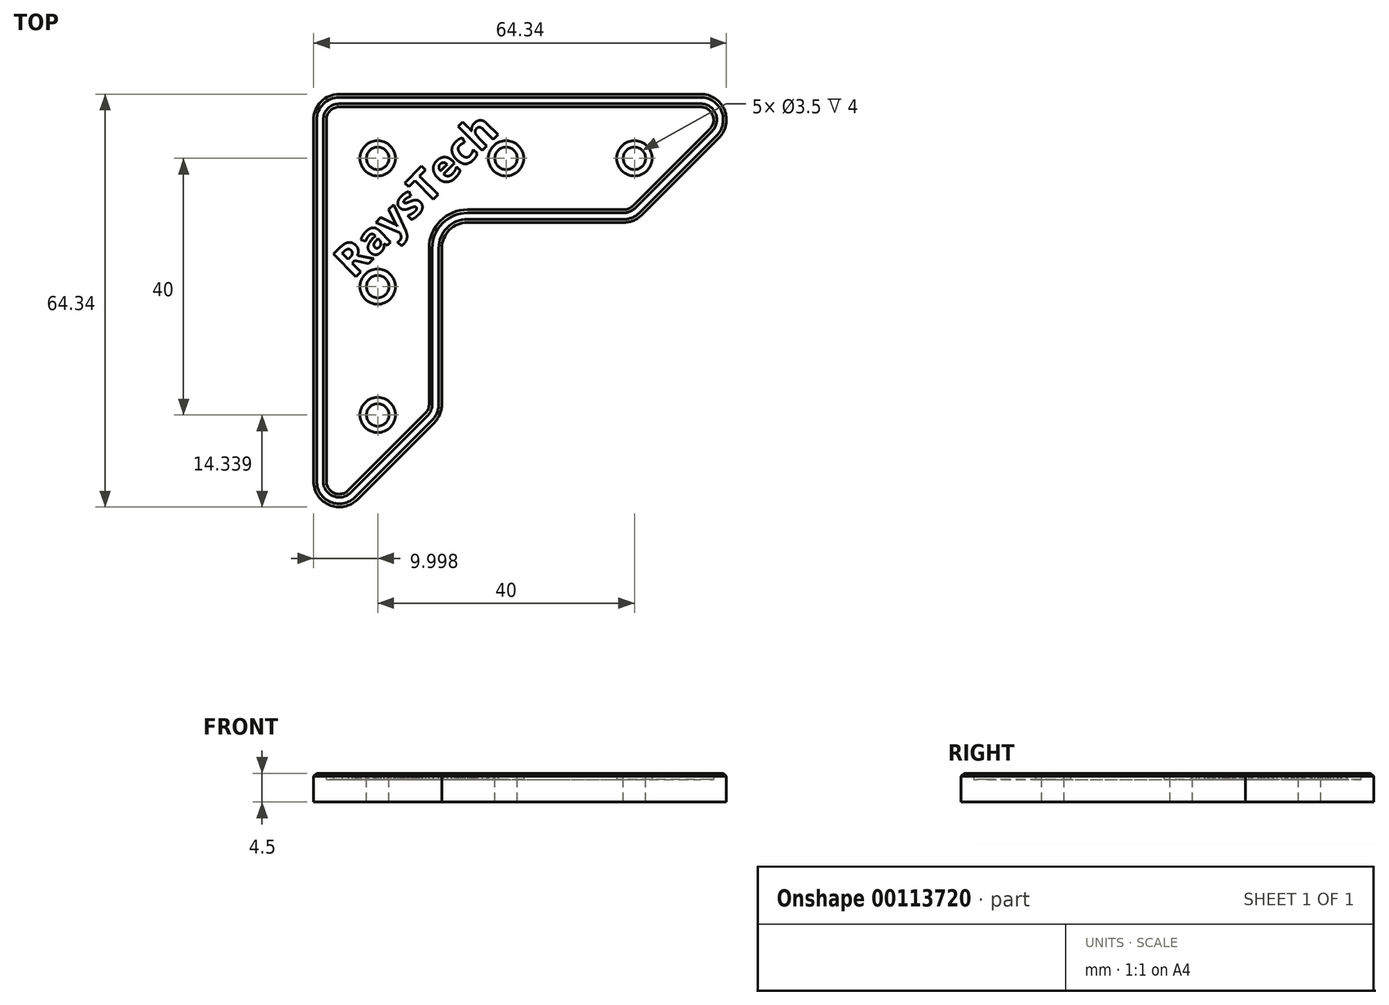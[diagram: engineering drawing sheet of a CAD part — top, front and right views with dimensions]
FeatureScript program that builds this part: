
annotation { "Feature Type Name" : "Feature", "Feature Type Description" : "" }
export const myFeature = defineFeature(function(context is Context, id is Id, definition is map)
    precondition{}
    {
        {
            var Q0;
            Q0=qCreatedBy(makeId("Top.planeOp"),FACE);
            var sketch = newSketch(context, id + "F0", { "sketchPlane" : qUnion([Q0])});
            skLineSegment(sketch, "E0", {"start": v(-45.73, 7.88) * mm, "end": v(24.27, 7.88) * mm});
            skLineSegment(sketch, "E1", {"start": v(24.27, 7.88) * mm, "end": v(4.27, -12.12) * mm});
            skLineSegment(sketch, "E2", {"start": v(-25.73, -42.12) * mm, "end": v(-45.73, -62.12) * mm});
            skLineSegment(sketch, "E3", {"start": v(-45.73, -62.12) * mm, "end": v(-45.73, 7.88) * mm});
            skLineSegment(sketch, "E4", {"start": v(-25.73, -42.12) * mm, "end": v(-25.73, -12.12) * mm});
            skLineSegment(sketch, "E5", {"start": v(-25.73, -12.12) * mm, "end": v(4.27, -12.12) * mm});
            skSolve(sketch);
        }
        {
            var Q0;
            Q0=makeQuery(id+"F0.imprint","IMPRINT",FACE,{"disambiguationData":[TD([[makeQuery(id+"F0.imprint","IMPRINT",EDGE,{"derivedFrom":sQuery(id+"F0.wireOp",EDGE,"E0")}),-1.0]])]});
            extrude(context, id + "F1", {"entities" : qUnion([Q0]), "depth" : 4.5 * mm});
        }
        {
            var Q0;
            Q0=makeQuery(id+"F1.opExtrude","SWEPT_EDGE",EDGE,{"disambiguationData":[OSD([sQuery(id+"F0.wireOp",EDGE,"E1"),sQuery(id+"F0.wireOp",EDGE,"UjIPxmgy-P11w-CRmJ-qTDb-78PK7ju40zVm")])]});
            var Q1;
            Q1=makeQuery(id+"F1.opExtrude","SWEPT_EDGE",EDGE,{"disambiguationData":[OSD([sQuery(id+"F0.wireOp",EDGE,"E0"),sQuery(id+"F0.wireOp",EDGE,"E1")])]});
            var Q2;
            Q2=makeQuery(id+"F1.opExtrude","SWEPT_EDGE",EDGE,{"disambiguationData":[OSD([sQuery(id+"F0.wireOp",EDGE,"UjIPxmgy-P11w-CRmJ-qTDb-78PK7ju40zVm"),sQuery(id+"F0.wireOp",EDGE,"E2")])]});
            var Q3;
            Q3=makeQuery(id+"F1.opExtrude","SWEPT_EDGE",EDGE,{"disambiguationData":[OSD([sQuery(id+"F0.wireOp",EDGE,"E2"),sQuery(id+"F0.wireOp",EDGE,"E3")])]});
            var Q4;
            Q4=makeQuery(id+"F1.opExtrude","SWEPT_EDGE",EDGE,{"disambiguationData":[OSD([sQuery(id+"F0.wireOp",EDGE,"E0"),sQuery(id+"F0.wireOp",EDGE,"E3")])]});
            var Q5;
            Q5=makeQuery(id+"F1.opExtrude","SWEPT_EDGE",EDGE,{"disambiguationData":[OSD([sQuery(id+"F0.wireOp",EDGE,"E4"),sQuery(id+"F0.wireOp",EDGE,"E5")])]});
            fillet(context, id + "F2", {"entities" : qUnion([Q0, Q1, Q2, Q3, Q4, Q5]), "radius" : 4 * mm, "tangentPropagation" : true, "allowEdgeOverflow" : false});
        }
        {
            var Q0;
            Q0=makeQuery(id+"F1.opExtrude","CAP_FACE",FACE,{"disambiguationData":[OSD([sQuery(id+"F0.wireOp",EDGE,"E0"),sQuery(id+"F0.wireOp",EDGE,"E1"),sQuery(id+"F0.wireOp",EDGE,"UjIPxmgy-P11w-CRmJ-qTDb-78PK7ju40zVm"),sQuery(id+"F0.wireOp",EDGE,"E2"),sQuery(id+"F0.wireOp",EDGE,"E3"),sQuery(id+"F0.wireOp",EDGE,"C6Fx3dh9-c8in-fARx-cpzI-npJOqKGzg0Yl"),sQuery(id+"F0.wireOp",EDGE,"EsrDFDjG-3fY6-RK6S-8BCX-MYxAuXix4LG8"),sQuery(id+"F0.wireOp",EDGE,"29485572-baa4-49c2-8979-b70eeb0ac028.0.1.0"),sQuery(id+"F0.wireOp",EDGE,"29485572-baa4-49c2-8979-b70eeb0ac028.1.0.0")])],"isStart":false});
            shell(context, id + "F3", {"entities" : qUnion([Q0]), "thickness" : 2 * mm});
        }
        {
            var Q0;
            Q0=makeQuery(id+"F3.opShell","OFFSET_FACE",FACE,{"disambiguationData":[OSD([sQuery(id+"F0.wireOp",EDGE,"E0"),sQuery(id+"F0.wireOp",EDGE,"E1"),sQuery(id+"F0.wireOp",EDGE,"UjIPxmgy-P11w-CRmJ-qTDb-78PK7ju40zVm"),sQuery(id+"F0.wireOp",EDGE,"E2"),sQuery(id+"F0.wireOp",EDGE,"E3")])]});
            extrude(context, id + "F4", {"entities" : qUnion([Q0]), "operationType" : NewBodyOperationType.ADD, "depth" : 1.5 * mm});
        }
        {
            var Q0;
            Q0=makeQuery(id+"F4.opExtrude","CAP_FACE",FACE,{"disambiguationData":[OSD([sQuery(id+"F0.wireOp",EDGE,"E0"),sQuery(id+"F0.wireOp",EDGE,"E1"),sQuery(id+"F0.wireOp",EDGE,"UjIPxmgy-P11w-CRmJ-qTDb-78PK7ju40zVm"),sQuery(id+"F0.wireOp",EDGE,"E2"),sQuery(id+"F0.wireOp",EDGE,"E3")])],"isStart":false});
            var sketch = newSketch(context, id + "F5", { "sketchPlane" : qUnion([Q0])});
            skCircle(sketch, "E6", {"center": v(-15.73, -2.12) * mm, "radius": 1.75 * mm});
            skCircle(sketch, "E7", {"center": v(-35.73, -2.12) * mm, "radius": 1.75 * mm});
            skCircle(sketch, "E8.0.1.0", {"center": v(-35.73, -22.12) * mm, "radius": 1.75 * mm});
            skCircle(sketch, "E8.0.2.0", {"center": v(-35.73, -42.12) * mm, "radius": 1.75 * mm});
            skLineSegment(sketch, "E8.direction1", {"start": v(-35.73, -2.12) * mm, "end": v(-10.73, -2.12) * mm, "construction": true});
            skLineSegment(sketch, "E8.direction2", {"start": v(-35.73, -2.12) * mm, "end": v(-35.73, -22.12) * mm, "construction": true});
            skCircle(sketch, "E9.1.0.0", {"center": v(4.27, -2.12) * mm, "radius": 1.75 * mm});
            skLineSegment(sketch, "E9.direction1", {"start": v(-15.73, -2.12) * mm, "end": v(4.27, -2.12) * mm, "construction": true});
            skSolve(sketch);
        }
        {
            var Q0;
            Q0=makeQuery(id+"F5.imprint","IMPRINT",FACE,{"disambiguationData":[TD([[makeQuery(id+"F5.imprint","IMPRINT",EDGE,{"derivedFrom":sQuery(id+"F5.wireOp",EDGE,"E7")}),1.0]])]});
            var Q1;
            Q1=makeQuery(id+"F5.imprint","IMPRINT",FACE,{"disambiguationData":[TD([[makeQuery(id+"F5.imprint","IMPRINT",EDGE,{"derivedFrom":sQuery(id+"F5.wireOp",EDGE,"E8.0.1.0")}),1.0]])]});
            var Q2;
            Q2=makeQuery(id+"F5.imprint","IMPRINT",FACE,{"disambiguationData":[TD([[makeQuery(id+"F5.imprint","IMPRINT",EDGE,{"derivedFrom":sQuery(id+"F5.wireOp",EDGE,"E8.0.2.0")}),1.0]])]});
            var Q3;
            Q3=makeQuery(id+"F5.imprint","IMPRINT",FACE,{"disambiguationData":[TD([[makeQuery(id+"F5.imprint","IMPRINT",EDGE,{"derivedFrom":sQuery(id+"F5.wireOp",EDGE,"E6")}),1.0]])]});
            var Q4;
            Q4=makeQuery(id+"F5.imprint","IMPRINT",FACE,{"disambiguationData":[TD([[makeQuery(id+"F5.imprint","IMPRINT",EDGE,{"derivedFrom":sQuery(id+"F5.wireOp",EDGE,"E9.1.0.0")}),1.0]])]});
            var Q5;
            {var subQ0=sQuery(id+"F5.wireOp",EDGE,"jdfTss7Z-eeok-K7Mz-7EB7-kjHeA2OweIvG");Q5=makeQuery(id+"F5.imprint","IMPRINT",FACE,{"disambiguationData":[TD([[makeQuery(id+"F5.imprint","IMPRINT",EDGE,{"derivedFrom":subQ0}),-1.0]])]});}
            var Q6;
            {var subQ0=sQuery(id+"F5.wireOp",EDGE,"wVgjnJG7-Rj5f-aFt5-ZZJF-KgTkhGcvRVXm");Q6=makeQuery(id+"F5.imprint","IMPRINT",FACE,{"disambiguationData":[TD([[makeQuery(id+"F5.imprint","IMPRINT",EDGE,{"derivedFrom":subQ0}),-1.0]])]});}
            var Q7;
            {var subQ6=sQuery(id+"F5.wireOp",EDGE,"RVy5OgC0-ICvm-M4ql-stZB-AabC2zsMiATY");var subQ7=sQuery(id+"F5.wireOp",EDGE,"YzS8Al7C-abLq-VzwT-fEGe-Yr6nG38xgNkX");var subQ8=makeQuery(id+"F5.imprint","INTERSECT",VERTEX,{"derivedFrom":[subQ7,subQ6]});Q7=makeQuery(id+"F5.imprint","IMPRINT",FACE,{"disambiguationData":[TD([[makeQuery(id+"F5.imprint","IMPRINT",EDGE,{"disambiguationData":[TD([[subQ8,1.0]])],"derivedFrom":subQ7}),1.0]])]});}
            var Q8;
            {var subQ0=sQuery(id+"F5.wireOp",EDGE,"0WaZ1QWw-uPjq-ZYtX-hp5S-Yz8MdkMCCtMi");var subQ1=sQuery(id+"F5.wireOp",EDGE,"DCd4uEQ3-UyTZ-W7Wa-zxVm-6Wi47DU6BRvu");var subQ2=makeQuery(id+"F5.imprint","INTERSECT",VERTEX,{"derivedFrom":[subQ1,subQ0]});Q8=makeQuery(id+"F5.imprint","IMPRINT",FACE,{"disambiguationData":[TD([[makeQuery(id+"F5.imprint","IMPRINT",EDGE,{"disambiguationData":[TD([[subQ2,1.0]])],"derivedFrom":subQ1}),-1.0]])]});}
            var Q9;
            {var subQ0=sQuery(id+"F5.wireOp",EDGE,"RVy5OgC0-ICvm-M4ql-stZB-AabC2zsMiATY");var subQ1=sQuery(id+"F5.wireOp",EDGE,"YzS8Al7C-abLq-VzwT-fEGe-Yr6nG38xgNkX");var subQ2=makeQuery(id+"F5.imprint","INTERSECT",VERTEX,{"derivedFrom":[subQ1,subQ0]});Q9=makeQuery(id+"F5.imprint","IMPRINT",FACE,{"disambiguationData":[TD([[makeQuery(id+"F5.imprint","IMPRINT",EDGE,{"disambiguationData":[TD([[subQ2,1.0]])],"derivedFrom":subQ1}),-1.0]])]});}
            extrude(context, id + "F6", {"entities" : qUnion([Q0, Q1, Q2, Q3, Q4, Q5, Q6, Q7, Q8, Q9]), "operationType" : NewBodyOperationType.REMOVE, "oppositeDirection" : true, "depth" : 25 * mm});
        }
        {
            var Q0;
            Q0=makeQuery(id+"F4.opExtrude","CAP_FACE",FACE,{"disambiguationData":[OSD([sQuery(id+"F0.wireOp",EDGE,"E0"),sQuery(id+"F0.wireOp",EDGE,"E1"),sQuery(id+"F0.wireOp",EDGE,"UjIPxmgy-P11w-CRmJ-qTDb-78PK7ju40zVm"),sQuery(id+"F0.wireOp",EDGE,"E2"),sQuery(id+"F0.wireOp",EDGE,"E3")])],"isStart":false});
            var sketch = newSketch(context, id + "F7", { "sketchPlane" : qUnion([Q0])});
            skText(sketch, "E10", { "text": "RaysTech", "fontName": "OpenSans-Bold.ttf"});
            skLineSegment(sketch, "E11", {"start": v(-35.73, -22.12) * mm, "end": v(-15.73, -2.12) * mm, "construction": true});
            const initialGuessF7  = {"E10": [-0.03956, -0.021, 0.7071, 0.7071, 0.005]};
            skSetInitialGuess(sketch, initialGuessF7);
            skSolve(sketch);
        }
        {
            var Q0;
            Q0=qSketchRegion(id+"F7",true);
            extrude(context, id + "F8", {"entities" : qUnion([Q0]), "operationType" : NewBodyOperationType.ADD, "depth" : 0.6 * mm});
        }
        {
            var Q0;
            {var subQ0=sQuery(id+"F0.wireOp",EDGE,"E0");Q0=makeQuery(id+"F3.opShell","OFFSET_EDGE",EDGE,{"disambiguationData":[OSD([subQ0]),TDD([makeQuery(id+"F1.opExtrude","CAP_EDGE",EDGE,{"disambiguationData":[OSD([subQ0])],"isStart":false})])]});}
            chamfer(context, id + "F9", {"entities" : qUnion([Q0]), "width" : 0.5 * mm, "tangentPropagation" : true});
        }
        {
            var Q0;
            Q0=makeQuery(id+"F1.opExtrude","CAP_EDGE",EDGE,{"disambiguationData":[OSD([sQuery(id+"F0.wireOp",EDGE,"E3")])],"isStart":false});
            chamfer(context, id + "F10", {"entities" : qUnion([Q0]), "width" : 0.5 * mm, "tangentPropagation" : true});
        }
        {
            var Q0;
            {var subQ0=sQuery(id+"F0.wireOp",EDGE,"E5");var subQ1=sQuery(id+"F0.wireOp",EDGE,"E3");var subQ2=sQuery(id+"F0.wireOp",EDGE,"E0");var subQ3=sQuery(id+"F0.wireOp",EDGE,"E1");var subQ4=sQuery(id+"F0.wireOp",EDGE,"E2");var subQ5=sQuery(id+"F0.wireOp",EDGE,"E4");Q0=makeQuery(id+"F8.boolean.opBoolean","SPLIT",FACE,{"disambiguationData":[TD([makeQuery(id+"F3.opShell","OFFSET_FACE",FACE,{"disambiguationData":[OSD([subQ2])]})])],"derivedFrom":makeQuery(id+"F4.opExtrude","CAP_FACE",FACE,{"disambiguationData":[OSD([subQ2,subQ3,subQ4,subQ1,subQ5,subQ0])],"isStart":false})});}
            var sketch = newSketch(context, id + "F11", { "sketchPlane" : qUnion([Q0])});
            skCircle(sketch, "E12", {"center": v(-35.73, -2.12) * mm, "radius": 2.75 * mm});
            skCircle(sketch, "E13.0.1.0", {"center": v(-35.73, -22.12) * mm, "radius": 2.75 * mm});
            skCircle(sketch, "E13.0.2.0", {"center": v(-35.73, -42.12) * mm, "radius": 2.75 * mm});
            skLineSegment(sketch, "E13.direction1", {"start": v(-35.73, -2.12) * mm, "end": v(-10.73, -2.12) * mm, "construction": true});
            skLineSegment(sketch, "E13.direction2", {"start": v(-35.73, -2.12) * mm, "end": v(-35.73, -22.12) * mm, "construction": true});
            skCircle(sketch, "E14.1.0.0", {"center": v(-15.73, -2.12) * mm, "radius": 2.75 * mm});
            skCircle(sketch, "E14.2.0.0", {"center": v(4.27, -2.12) * mm, "radius": 2.75 * mm});
            skLineSegment(sketch, "E14.direction1", {"start": v(-35.73, -2.12) * mm, "end": v(-15.73, -2.12) * mm, "construction": true});
            skSolve(sketch);
        }
        {
            var Q0;
            Q0=makeQuery(id+"F11.imprint","IMPRINT",FACE,{"disambiguationData":[TD([[makeQuery(id+"F11.imprint","IMPRINT",EDGE,{"derivedFrom":sQuery(id+"F11.wireOp",EDGE,"E12")}),1.0]])]});
            var Q1;
            Q1=makeQuery(id+"F11.imprint","IMPRINT",FACE,{"disambiguationData":[TD([[makeQuery(id+"F11.imprint","IMPRINT",EDGE,{"derivedFrom":sQuery(id+"F11.wireOp",EDGE,"E13.0.1.0")}),1.0]])]});
            var Q2;
            Q2=makeQuery(id+"F11.imprint","IMPRINT",FACE,{"disambiguationData":[TD([[makeQuery(id+"F11.imprint","IMPRINT",EDGE,{"derivedFrom":sQuery(id+"F11.wireOp",EDGE,"E13.0.2.0")}),1.0]])]});
            var Q3;
            Q3=makeQuery(id+"F11.imprint","IMPRINT",FACE,{"disambiguationData":[TD([[makeQuery(id+"F11.imprint","IMPRINT",EDGE,{"derivedFrom":sQuery(id+"F11.wireOp",EDGE,"E14.1.0.0")}),1.0]])]});
            var Q4;
            Q4=makeQuery(id+"F11.imprint","IMPRINT",FACE,{"disambiguationData":[TD([[makeQuery(id+"F11.imprint","IMPRINT",EDGE,{"derivedFrom":sQuery(id+"F11.wireOp",EDGE,"E14.2.0.0")}),1.0]])]});
            extrude(context, id + "F12", {"entities" : qUnion([Q0, Q1, Q2, Q3, Q4]), "operationType" : NewBodyOperationType.ADD, "depth" : 0.5 * mm});
        }
    });
